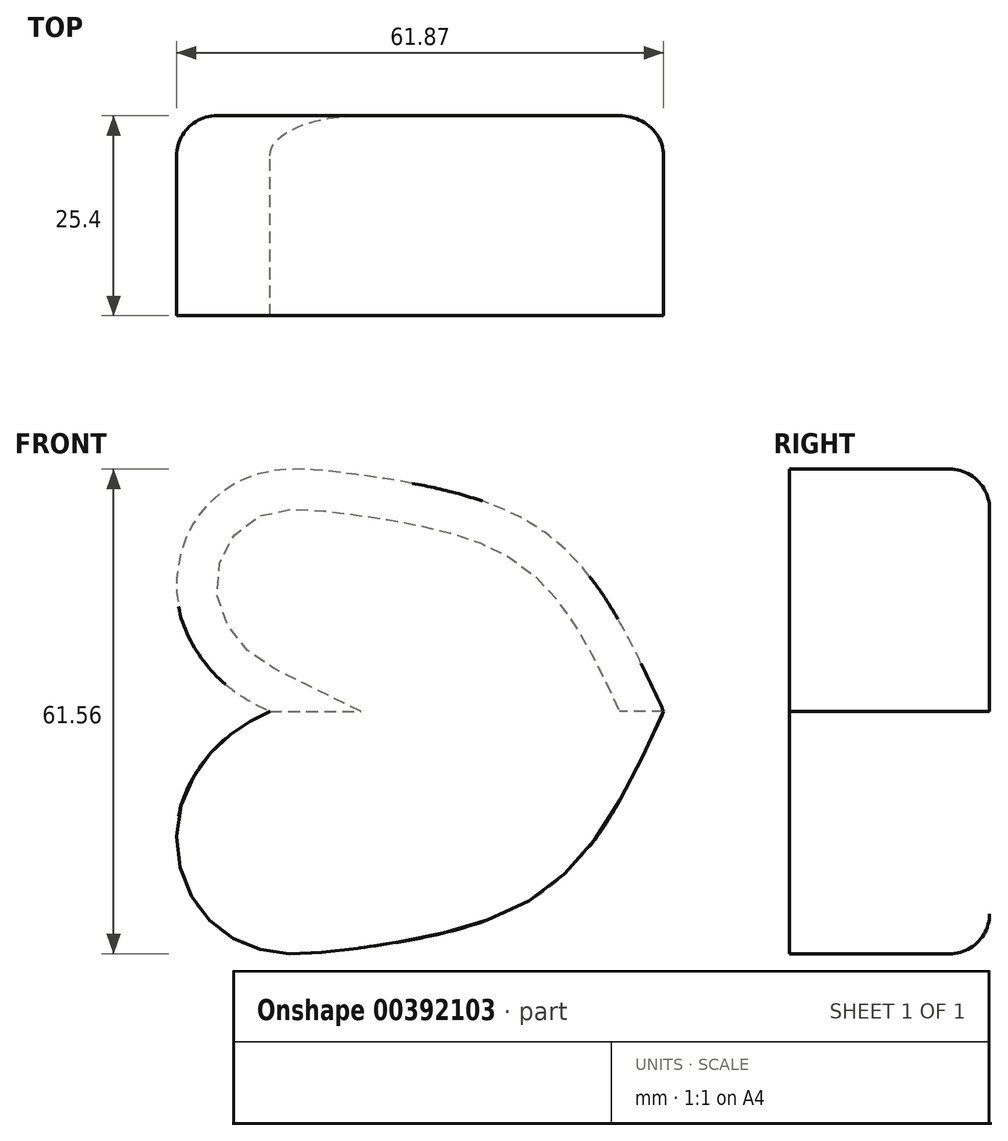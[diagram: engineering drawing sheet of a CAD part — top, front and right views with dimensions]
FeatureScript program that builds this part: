
annotation { "Feature Type Name" : "Feature", "Feature Type Description" : "" }
export const myFeature = defineFeature(function(context is Context, id is Id, definition is map)
    precondition{}
    {
        {
            var Q0;
            Q0=qCreatedBy(makeId("Front.planeOp"),FACE);
            var sketch = newSketch(context, id + "F0", { "sketchPlane" : qUnion([Q0])});
            skFitSpline(sketch, "E0", {"points": [v(39.57, 0) * mm, v(24.46, 22.73) * mm, v(1.24, 30) * mm, v(-12, 30.14) * mm, v(-20.27, 23.73) * mm, v(-21.84, 12.33) * mm, v(-16.14, 3.5) * mm, v(-10.44, 0) * mm], "startDerivative": vector(-60.7, 133.04) * mm, "endDerivative": vector(57.86, -28.31) * mm});
            skFitSpline(sketch, "E1.MirrorCS", {"points": [v(39.57, 0) * mm, v(24.46, -22.73) * mm, v(1.24, -30) * mm, v(-12, -30.14) * mm, v(-20.27, -23.73) * mm, v(-21.84, -12.33) * mm, v(-16.14, -3.5) * mm, v(-10.44, 0) * mm], "startDerivative": vector(-60.7, -133.04) * mm, "endDerivative": vector(57.86, 28.31) * mm});
            skSolve(sketch);
        }
        {
            var Q0;
            Q0=makeQuery(id+"F0.imprint","IMPRINT",FACE,{"disambiguationData":[TD([[makeQuery(id+"F0.imprint","IMPRINT",EDGE,{"derivedFrom":sQuery(id+"F0.wireOp",EDGE,"E0")}),1.0]])]});
            extrude(context, id + "F1", {"entities" : qUnion([Q0]), "depth" : 25.4 * mm});
        }
        {
            var Q0;
            Q0=makeQuery(id+"F1.opExtrude","CAP_FACE",FACE,{"disambiguationData":[OSD([sQuery(id+"F0.wireOp",EDGE,"E0"),sQuery(id+"F0.wireOp",EDGE,"E1.MirrorCS")])],"isStart":true});
            fillet(context, id + "F2", {"entities" : qUnion([Q0]), "radius" : 5.08 * mm, "tangentPropagation" : true, "allowEdgeOverflow" : false});
        }
    });
